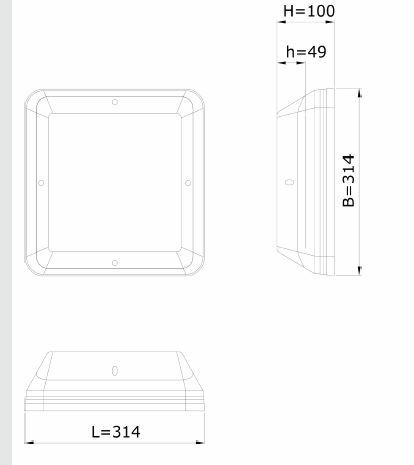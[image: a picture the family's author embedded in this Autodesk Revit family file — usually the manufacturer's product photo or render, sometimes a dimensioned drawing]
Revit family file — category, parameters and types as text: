
# Revit family: Lightronics_LightingFixture_WallAndCeiling_TPB1
name_source: partatom
category: Lighting Fixtures
revit_build: Autodesk Revit 2016 (Build: 20160314_0715(x64)
units: mm (PartAtom-declared; Revit-internal decimal feet)

## family parameters
Cut with Voids When Loaded = No
Host = Face
Light Source = Yes
OmniClass Number = 23.80.70.00
OmniClass Title = Lighting
Part Type = Normal
Room Calculation Point = No
Round Connector Dimension = Use Diameter
Shared = No

## types (1)
- TPS
    Apparent Load = 0 VA
    Assembly Code = D5020200
    AssetType = Fixed
    BIMObjectName = Lightronics_LightingFixture_WallAndCeiling_TPB
    ClassificationName = Uniclass 2015
    ClassificationValue = Pr_70_70_48_85
    Color = Housing: impactproof, flame-retardent, UV-stabilised polycarbonate in white RAL 9010, black RAL 9005 or anthracite RAL7016. Cover: polycarbonate lens, clear prismatic, opal or frosted
    Color Filter = 16777215
    Default Elevation = 1219 mm
    Depth = 314 mm  [stored 1.03018 ft]
    Description = The TPB is a versatile and compact surface-mounted luminaire with very high light output. The TPB luminaire's housing is impactproof and flame-retardant. It can be fitted with up to three light sources. The TPB can also be easily used as emergency lighting.
    Dimming Lamp Color Temperature Shift = <None>
    DocumentationLiterature = https://specifi.bimstore.co.uk
    DurationUnit = 20 Years
    Emit Shape Visible in Rendering = No
    Emit from Rectangle Length = 250 mm  [stored 0.82021 ft]
    Emit from Rectangle Width = 250 mm  [stored 0.82021 ft]
    ExpectedLife = 10
    Height = 100 mm  [stored 0.328084 ft]
    IfcExportAs = IfcLightFixtureTypeEnum.POINTSOURCE
    IfcExportType = IfcLightFixture
    Keynote = V90/510
    Length = 314 mm  [stored 1.03018 ft]
    Manufacturer = Lightronics
    ManufacturerName = Lightronics
    Material = Impact proof, flame-retardant, UV-stabilised polycarbonate
    Model = TPB
    ModelNumber = TPB
    ModelReference = IP 65
    NBSDescription = Surface luminaires
    NBSObjectName = Lightronics -  General purpose luminaires
    NBSReference = 90-60-50/405
    NominalDepth = 314 mm  [stored 1.03018 ft]
    NominalHeight = 100 mm  [stored 0.328084 ft]
    NominalLength = 314 mm  [stored 1.03018 ft]
    NumberOfPoles = 1
    Photometric Web File = TPB-OL4-32-6-180-D-F-650-230-X-W.ies
    ProductionYear = 2018
    Shape = Square
    Size = 314x314x100
    Tilt Angle = 90.00°
    Type Comments = Wall and ceiling lighting – Impactproof. Functional and stylishly designed
    TypeName = TPB
    URL = https://www.lightronics.nl
    Voltage = 230 V
    WarrantyDurationParts = 5
    WarrantyDurationUnit = Years
    _BSBibleVersion = 15
    _BimSpecGuid = 0
    _CurrentRevision = 1
    _DistributedBy = www.bimstore.co.uk

note: [stored X ft] marks values corroborated as IEEE doubles in the binary element streams (Revit-internal decimal feet)

## geometry (parser evidence)
native form markers: Sweep x3
no freeform markers — native parametric forms only
